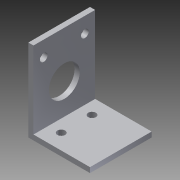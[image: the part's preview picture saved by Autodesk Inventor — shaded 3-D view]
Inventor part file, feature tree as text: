
AUTODESK INVENTOR PART (.ipt)
format: ipt  version: 2013 (Build 170138000, 138)  size: 109,056 bytes
history: native  units: in
note: dims shown in document units (in); Inventor stores cm internally (conversion verified against a paired STEP export)
features: extrude x3, sketch x3
ambient origin geometry x8: Origin, YZ Plane, XZ Plane, XY Plane, X Axis, Y Axis, Z Axis, Center Point
bodies: Solid1 (feature_tree)
feature tree (6):
  extrude  "Extrusion1"  Depth=2.0in
  extrude  "Extrusion2"  Depth=1.5in TaperAngle=0.0deg
  extrude  "Extrusion3"  Depth=0.375in
  sketch  "Sketch1"  dims[d0=1.5in d1=2.0in]
  sketch  "Sketch2"  dims[d2=0.125in d3=1.5in d4=0.0in]
  sketch  "Sketch3"  dims[d5=1.0in d6=0.375in d7=0.1875in d8=0.1875in d9=1.5in d10=0.0in d11=0.75in d12=0.875in d13=0.75in d17=0.1875in d18=0.425in d19=1.0in d20=0.0in]
